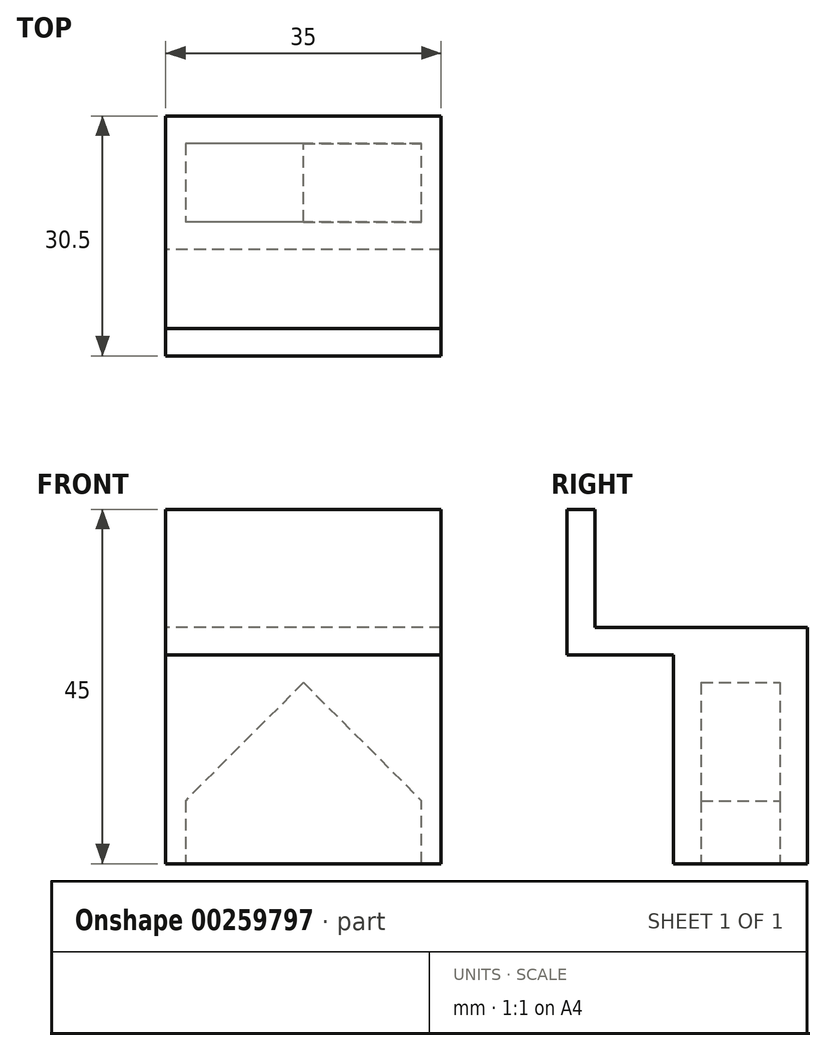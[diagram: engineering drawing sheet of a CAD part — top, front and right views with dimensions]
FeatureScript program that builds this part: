
annotation { "Feature Type Name" : "Feature", "Feature Type Description" : "" }
export const myFeature = defineFeature(function(context is Context, id is Id, definition is map)
    precondition{}
    {
        {
            var Q0;
            Q0=qCreatedBy(makeId("Right.planeOp"),FACE);
            var sketch = newSketch(context, id + "F0", { "sketchPlane" : qUnion([Q0])});
            skLineSegment(sketch, "E0", {"start": v(-22, 18.5) * mm, "end": v(-18.5, 18.5) * mm});
            skLineSegment(sketch, "E1", {"start": v(-18.5, 18.5) * mm, "end": v(-18.5, 3.5) * mm});
            skLineSegment(sketch, "E2", {"start": v(-18.5, 3.5) * mm, "end": v(8.5, 3.5) * mm});
            skLineSegment(sketch, "E3", {"start": v(8.5, 3.5) * mm, "end": v(8.5, -26.5) * mm});
            skLineSegment(sketch, "E4", {"start": v(8.5, -26.5) * mm, "end": v(-8.5, -26.5) * mm});
            skLineSegment(sketch, "E5", {"start": v(-8.5, -26.5) * mm, "end": v(-8.5, 0) * mm});
            skLineSegment(sketch, "E6", {"start": v(-8.5, 0) * mm, "end": v(-22, 0) * mm});
            skLineSegment(sketch, "E7", {"start": v(-22, 0) * mm, "end": v(-22, 18.5) * mm});
            skSolve(sketch);
        }
        {
            var Q0;
            Q0=makeQuery(id+"F0.imprint","IMPRINT",FACE,{"disambiguationData":[TD([[makeQuery(id+"F0.imprint","IMPRINT",EDGE,{"derivedFrom":sQuery(id+"F0.wireOp",EDGE,"E0")}),-1.0]])]});
            extrude(context, id + "F1", {"entities" : qUnion([Q0]), "depth" : 35 * mm, "offsetDistance" : 25 * mm, "symmetric" : true});
        }
        {
            var Q0;
            Q0=qCreatedBy(makeId("Front.planeOp"),FACE);
            var sketch = newSketch(context, id + "F2", { "sketchPlane" : qUnion([Q0])});
            skLineSegment(sketch, "E8", {"start": v(0, -3.5) * mm, "end": v(-15, -18.5) * mm});
            skLineSegment(sketch, "E9", {"start": v(0, -3.5) * mm, "end": v(15, -18.5) * mm});
            skLineSegment(sketch, "E10", {"start": v(-15, -18.5) * mm, "end": v(-15, -27.2) * mm});
            skLineSegment(sketch, "E11", {"start": v(-15, -27.2) * mm, "end": v(15, -27.2) * mm});
            skLineSegment(sketch, "E12", {"start": v(15, -27.2) * mm, "end": v(15, -18.5) * mm});
            skSolve(sketch);
        }
        {
            var Q0;
            Q0=makeQuery(id+"F2.imprint","IMPRINT",FACE,{"disambiguationData":[TD([[makeQuery(id+"F2.imprint","IMPRINT",EDGE,{"derivedFrom":sQuery(id+"F2.wireOp",EDGE,"E8")}),1.0]])]});
            extrude(context, id + "F3", {"entities" : qUnion([Q0]), "operationType" : NewBodyOperationType.REMOVE, "depth" : 10 * mm, "offsetDistance" : 25 * mm, "symmetric" : true});
        }
    });
